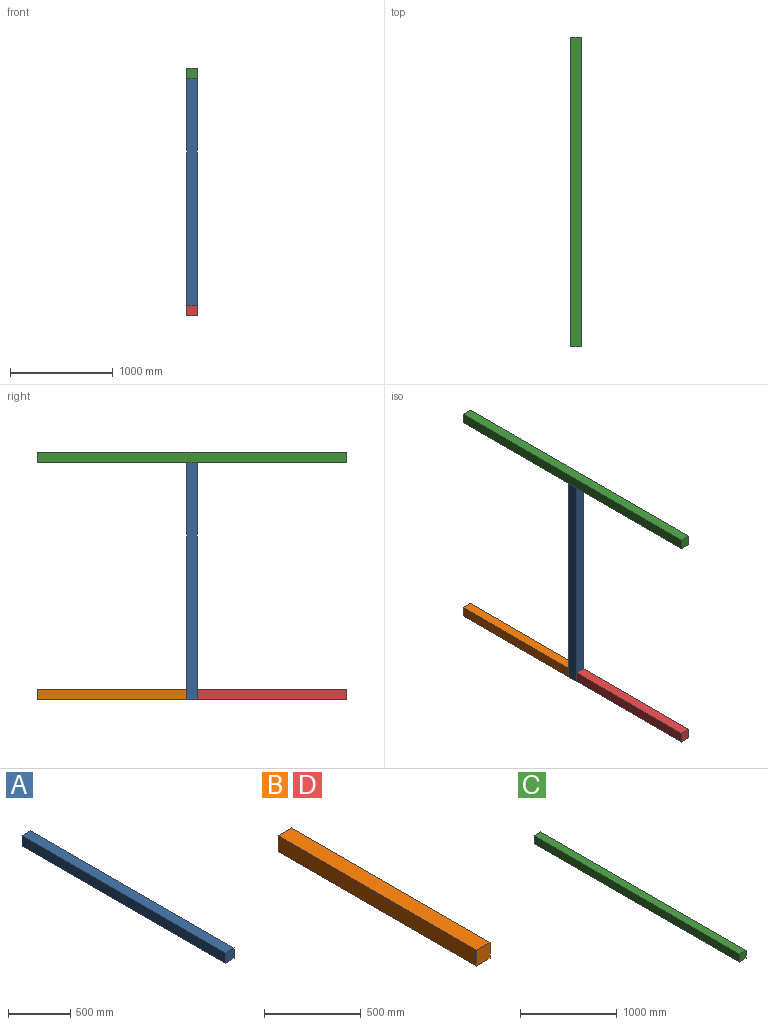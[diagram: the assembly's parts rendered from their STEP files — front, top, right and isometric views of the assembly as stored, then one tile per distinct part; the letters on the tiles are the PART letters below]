
ASSEMBLY  parts=4 mates=3
PART A: 6 faces, bbox 100x2300x100 mm
  f0: plane 2300x100mm, normal (-1,0,0), area 230000mm2, adj f1,f3,f4,f5
  f1: plane 2300x100mm, normal (0,0,-1), area 230000mm2, adj f0,f2,f4,f5
  f2: plane 2300x100mm, normal (1,0,0), area 230000mm2, adj f1,f3,f4,f5
  f3: plane 2300x100mm, normal (0,0,1), area 230000mm2, adj f0,f2,f4,f5
  f4: plane 100x100mm, normal (0,-1,0), area 10000mm2, adj f0,f1,f2,f3
  f5: plane 100x100mm, normal (0,1,0), area 10000mm2, adj f0,f1,f2,f3
PART B: 6 faces, bbox 100x1450x100 mm
  f0: plane 100x100mm, normal (0,-1,0), area 10000mm2, adj f1,f3,f4,f5
  f1: plane 1450x100mm, normal (0,0,-1), area 145000mm2, adj f0,f2,f3,f4
  f2: plane 100x100mm, normal (0,1,0), area 10000mm2, adj f1,f3,f4,f5
  f3: plane 1450x100mm, normal (1,0,0), area 145000mm2, adj f0,f1,f2,f5
  f4: plane 1450x100mm, normal (-1,0,0), area 145000mm2, adj f0,f1,f2,f5
  f5: plane 1450x100mm, normal (0,0,1), area 145000mm2, adj f0,f2,f3,f4
PART C: 6 faces, bbox 100x3000x100 mm
  f0: plane 3000x100mm, normal (-1,0,0), area 300000mm2, adj f1,f3,f4,f5
  f1: plane 3000x100mm, normal (0,0,-1), area 300000mm2, adj f0,f2,f4,f5
  f2: plane 3000x100mm, normal (1,0,0), area 300000mm2, adj f1,f3,f4,f5
  f3: plane 3000x100mm, normal (0,0,1), area 300000mm2, adj f0,f2,f4,f5
  f4: plane 100x100mm, normal (0,-1,0), area 10000mm2, adj f0,f1,f2,f3
  f5: plane 100x100mm, normal (0,1,0), area 10000mm2, adj f0,f1,f2,f3
PART D: same geometry as B
PLACE A rot(axis=(-1,0,0),90deg) t=(-100,1450,-2300)mm
PLACE B t=(-100,3000,-2300)mm
PLACE C t=(-100,3000,0)mm
PLACE D t=(-100,1450,-2300)mm
MATE fastened A.f4 <-> C.f1  axis (0,0,1) through (0,1500,0)mm
MATE fastened B.f0 <-> A.f3  axis (0,-1,0) through (0,1550,-2300)mm
MATE fastened D.f2 <-> A.f1  axis (0,1,0) through (0,1450,-2300)mm
